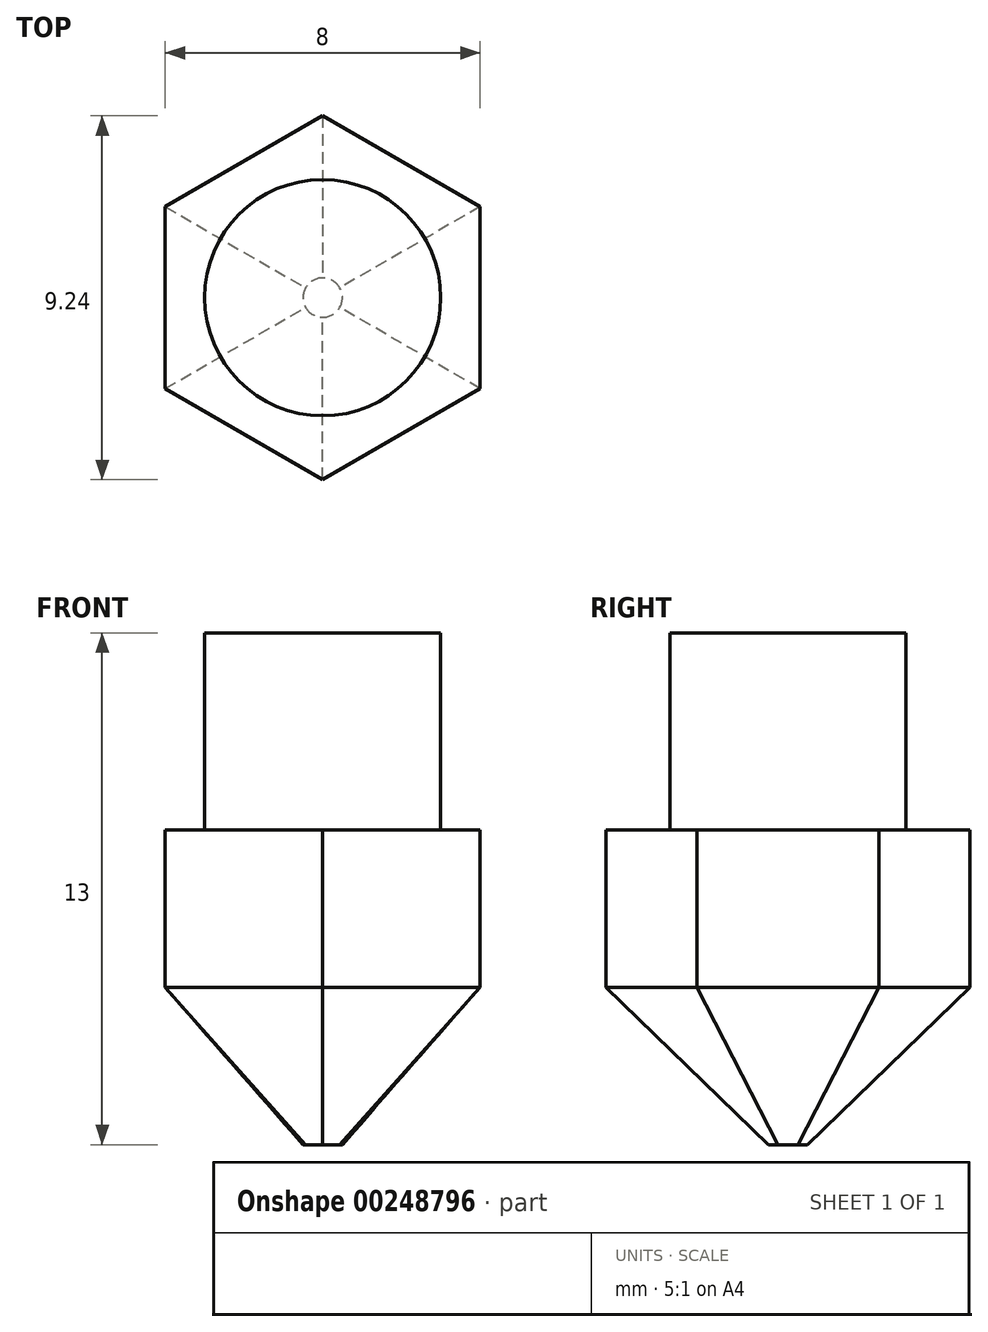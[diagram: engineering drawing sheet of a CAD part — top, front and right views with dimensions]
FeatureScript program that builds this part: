
annotation { "Feature Type Name" : "Feature", "Feature Type Description" : "" }
export const myFeature = defineFeature(function(context is Context, id is Id, definition is map)
    precondition{}
    {
        {
            var Q0;
            Q0=qCreatedBy(makeId("Top.planeOp"),FACE);
            var sketch = newSketch(context, id + "F0", { "sketchPlane" : qUnion([Q0])});
            skCircle(sketch, "E0", {"center": v(0, 0) * mm, "radius": 3 * mm});
            skCircle(sketch, "E1.cCircle", {"center": v(0, 0) * mm, "radius": 4 * mm, "construction": true});
            skLineSegment(sketch, "E1.0", {"start": v(4, 2.3) * mm, "end": v(4, -2.3) * mm});
            skLineSegment(sketch, "E1.1", {"start": v(4, -2.3) * mm, "end": v(0, -4.62) * mm});
            skLineSegment(sketch, "E1.2", {"start": v(0, -4.62) * mm, "end": v(-4, -2.3) * mm});
            skLineSegment(sketch, "E1.3", {"start": v(-4, -2.3) * mm, "end": v(-4, 2.3) * mm});
            skLineSegment(sketch, "E1.4", {"start": v(-4, 2.3) * mm, "end": v(0, 4.62) * mm});
            skLineSegment(sketch, "E1.5", {"start": v(0, 4.62) * mm, "end": v(4, 2.3) * mm});
            skPoint(sketch, "E1.0.midPoint", {"position": v(4, 0) * mm});
            skSolve(sketch);
        }
        {
            var Q0;
            Q0=makeQuery(id+"F0.imprint","IMPRINT",FACE,{"disambiguationData":[TD([[makeQuery(id+"F0.imprint","IMPRINT",EDGE,{"derivedFrom":sQuery(id+"F0.wireOp",EDGE,"E0")}),1.0]])]});
            extrude(context, id + "F1", {"entities" : qUnion([Q0]), "depth" : 5 * mm, "offsetDistance" : 25 * mm});
        }
        {
            var Q0;
            Q0=makeQuery(id+"F0.imprint","IMPRINT",FACE,{"disambiguationData":[TD([[makeQuery(id+"F0.imprint","IMPRINT",EDGE,{"derivedFrom":sQuery(id+"F0.wireOp",EDGE,"E0")}),-1.0]])]});
            var Q1;
            Q1=makeQuery(id+"F0.imprint","IMPRINT",FACE,{"disambiguationData":[TD([[makeQuery(id+"F0.imprint","IMPRINT",EDGE,{"derivedFrom":sQuery(id+"F0.wireOp",EDGE,"E0")}),1.0]])]});
            extrude(context, id + "F2", {"entities" : qUnion([Q0, Q1]), "operationType" : NewBodyOperationType.ADD, "oppositeDirection" : true, "depth" : 4 * mm, "offsetDistance" : 25 * mm});
        }
        {
            var Q0;
            Q0=makeQuery(id+"F1.opExtrude","CAP_FACE",FACE,{"disambiguationData":[OSD([sQuery(id+"F0.wireOp",EDGE,"E0")])],"isStart":false});
            cPlane(context, id + "F3", {"entities" : qUnion([Q0]), "cplaneType" : CPlaneType.OFFSET, "offset" : 13 * mm, "oppositeDirection" : true, "width" : 150 * mm, "height" : 150 * mm});
        }
        {
            var Q0;
            Q0=qCreatedBy(id+"F3.planeOp",FACE);
            var sketch = newSketch(context, id + "F4", { "sketchPlane" : qUnion([Q0])});
            skCircle(sketch, "E2", {"center": v(0, 0) * mm, "radius": 0.5 * mm});
            skSolve(sketch);
        }
        {
            var Q1;
            Q1=makeQuery(id+"F2.opExtrude","CAP_FACE",FACE,{"disambiguationData":[OSD([sQuery(id+"F0.wireOp",EDGE,"E1.0"),sQuery(id+"F0.wireOp",EDGE,"E1.1"),sQuery(id+"F0.wireOp",EDGE,"E1.2"),sQuery(id+"F0.wireOp",EDGE,"E1.3"),sQuery(id+"F0.wireOp",EDGE,"E1.4"),sQuery(id+"F0.wireOp",EDGE,"E1.5")])],"isStart":false});
            var Q2;
            Q2=makeQuery(id+"F4.imprint","IMPRINT",FACE,{"disambiguationData":[TD([[makeQuery(id+"F4.imprint","IMPRINT",EDGE,{"derivedFrom":sQuery(id+"F4.wireOp",EDGE,"E2")}),1.0]])]});
            loft(context, id + "F5", {"operationType" : NewBodyOperationType.ADD, "sheetProfilesArray" : [{ "sheetProfileEntities" : qUnion([Q1]) }, { "sheetProfileEntities" : qUnion([Q2]) }]});
        }
    });
